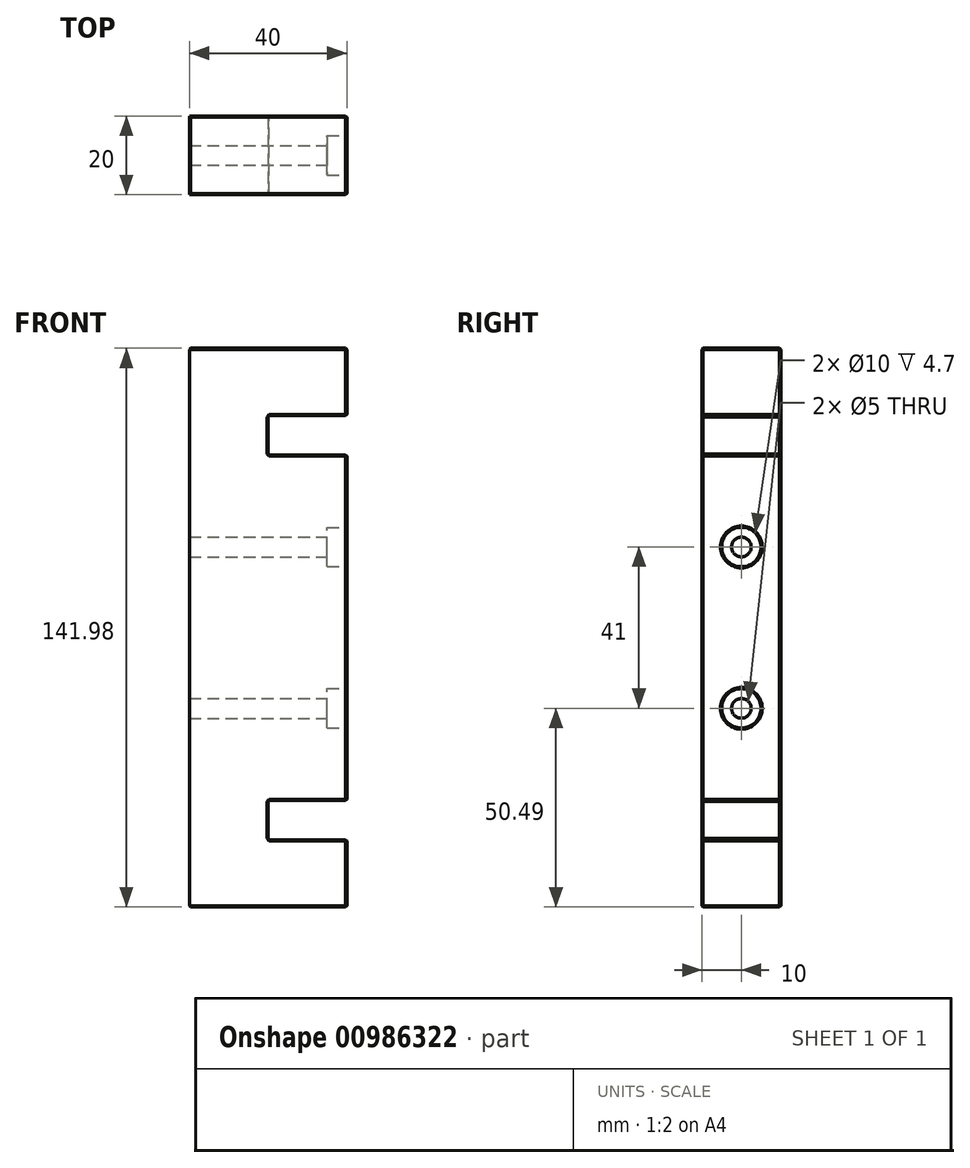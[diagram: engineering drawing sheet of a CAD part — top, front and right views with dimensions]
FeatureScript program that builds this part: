
annotation { "Feature Type Name" : "Feature", "Feature Type Description" : "" }
export const myFeature = defineFeature(function(context is Context, id is Id, definition is map)
    precondition{}
    {
        {
            var Q0;
            Q0=qCreatedBy(makeId("Right.planeOp"),FACE);
            var sketch = newSketch(context, id + "F0", { "sketchPlane" : qUnion([Q0])});
            skLineSegment(sketch, "E0", {"start": v(0, 0) * mm, "end": v(10, 0) * mm});
            skLineSegment(sketch, "E1", {"start": v(10, 0) * mm, "end": v(10, 141.98) * mm});
            skLineSegment(sketch, "E2", {"start": v(10, 141.98) * mm, "end": v(-10, 141.98) * mm});
            skLineSegment(sketch, "E3", {"start": v(-10, 141.98) * mm, "end": v(-10, 0) * mm});
            skLineSegment(sketch, "E4", {"start": v(-10, 0) * mm, "end": v(0, 0) * mm});
            skSolve(sketch);
        }
        {
            var Q0;
            Q0=makeQuery(id+"F0.imprint","IMPRINT",FACE,{"disambiguationData":[TD([[makeQuery(id+"F0.imprint","IMPRINT",EDGE,{"derivedFrom":sQuery(id+"F0.wireOp",EDGE,"E0")}),1.0]])]});
            extrude(context, id + "F1", {"entities" : qUnion([Q0]), "oppositeDirection" : true, "depth" : 40 * mm, "offsetDistance" : 25 * mm});
        }
        {
            var Q0;
            Q0=qCreatedBy(makeId("Right.planeOp"),FACE);
            var sketch = newSketch(context, id + "F2", { "sketchPlane" : qUnion([Q0])});
            skLineSegment(sketch, "E5", {"start": v(0, 0) * mm, "end": v(0, 50.5) * mm});
            skLineSegment(sketch, "E6", {"start": v(0, 50.5) * mm, "end": v(0, 91.49) * mm});
            skCircle(sketch, "E7", {"center": v(0, 50.5) * mm, "radius": 5 * mm});
            skCircle(sketch, "E8", {"center": v(0, 91.49) * mm, "radius": 5 * mm});
            skCircle(sketch, "E9", {"center": v(0, 91.49) * mm, "radius": 2.5 * mm});
            skCircle(sketch, "E10", {"center": v(0, 50.5) * mm, "radius": 2.5 * mm});
            skSolve(sketch);
        }
        {
            var Q0;
            Q0=makeQuery(id+"F2.imprint","IMPRINT",FACE,{"disambiguationData":[TD([[makeQuery(id+"F2.imprint","IMPRINT",EDGE,{"derivedFrom":sQuery(id+"F2.wireOp",EDGE,"E8")}),1.0]])]});
            var Q1;
            {var subQ0=sQuery(id+"F2.wireOp",EDGE,"E7");var subQ1=sQuery(id+"F2.wireOp",EDGE,"E5");var subQ2=makeQuery(id+"F2.imprint","INTERSECT",VERTEX,{"derivedFrom":[subQ1,subQ0]});Q1=makeQuery(id+"F2.imprint","IMPRINT",FACE,{"disambiguationData":[TD([[makeQuery(id+"F2.imprint","IMPRINT",EDGE,{"disambiguationData":[TD([[subQ2,-1.0]])],"derivedFrom":subQ1}),-1.0]])]});}
            var Q2;
            {var subQ0=sQuery(id+"F2.wireOp",EDGE,"E7");var subQ1=sQuery(id+"F2.wireOp",EDGE,"E5");var subQ2=makeQuery(id+"F2.imprint","INTERSECT",VERTEX,{"derivedFrom":[subQ1,subQ0]});Q2=makeQuery(id+"F2.imprint","IMPRINT",FACE,{"disambiguationData":[TD([[makeQuery(id+"F2.imprint","IMPRINT",EDGE,{"disambiguationData":[TD([[subQ2,-1.0]])],"derivedFrom":subQ1}),1.0]])]});}
            extrude(context, id + "F3", {"entities" : qUnion([Q0, Q1, Q2]), "operationType" : NewBodyOperationType.REMOVE, "oppositeDirection" : true, "depth" : 5 * mm, "offsetDistance" : 25 * mm});
        }
        {
            var Q0;
            Q0=makeQuery(id+"F3.boolean.opBoolean","SPLIT",FACE,{"disambiguationData":[TD([makeQuery(id+"F3.opExtrude","SWEPT_FACE",FACE,{"disambiguationData":[OSD([sQuery(id+"F2.wireOp",EDGE,"E9")])]})])],"derivedFrom":makeQuery(id+"F1.opExtrude","CAP_FACE",FACE,{"disambiguationData":[OSD([sQuery(id+"F0.wireOp",EDGE,"E0"),sQuery(id+"F0.wireOp",EDGE,"E1"),sQuery(id+"F0.wireOp",EDGE,"E2"),sQuery(id+"F0.wireOp",EDGE,"E3"),sQuery(id+"F0.wireOp",EDGE,"E4")])],"isStart":true})});
            var Q1;
            Q1=makeQuery(id+"F3.boolean.opBoolean","SPLIT",FACE,{"disambiguationData":[TD([makeQuery(id+"F3.opExtrude","SWEPT_FACE",FACE,{"disambiguationData":[OSD([sQuery(id+"F2.wireOp",EDGE,"E10")])]})])],"derivedFrom":makeQuery(id+"F1.opExtrude","CAP_FACE",FACE,{"disambiguationData":[OSD([sQuery(id+"F0.wireOp",EDGE,"E0"),sQuery(id+"F0.wireOp",EDGE,"E1"),sQuery(id+"F0.wireOp",EDGE,"E2"),sQuery(id+"F0.wireOp",EDGE,"E3"),sQuery(id+"F0.wireOp",EDGE,"E4")])],"isStart":true})});
            extrude(context, id + "F4", {"entities" : qUnion([Q0, Q1]), "operationType" : NewBodyOperationType.REMOVE, "endBound" : BoundingType.THROUGH_ALL, "oppositeDirection" : true, "depth" : 25 * mm, "offsetDistance" : 25 * mm});
        }
        {
            var Q0;
            Q0=makeQuery(id+"F1.opExtrude","SWEPT_FACE",FACE,{"disambiguationData":[OSD([sQuery(id+"F0.wireOp",EDGE,"E3")])]});
            cPlane(context, id + "F5", {"entities" : qUnion([Q0]), "cplaneType" : CPlaneType.OFFSET, "offset" : 0 * mm, "width" : 150 * mm, "height" : 150 * mm});
        }
        {
            var Q0;
            Q0=qCreatedBy(id+"F5.planeOp",FACE);
            var sketch = newSketch(context, id + "F6", { "sketchPlane" : qUnion([Q0])});
            skLineSegment(sketch, "E11", {"start": v(0, 0) * mm, "end": v(0, 17.1) * mm});
            skLineSegment(sketch, "E12", {"start": v(0, 17.1) * mm, "end": v(-20, 17.1) * mm});
            skLineSegment(sketch, "E13", {"start": v(-20, 17.1) * mm, "end": v(-20, 27.1) * mm});
            skLineSegment(sketch, "E14", {"start": v(-20, 27.1) * mm, "end": v(0, 27.1) * mm});
            skLineSegment(sketch, "E15", {"start": v(0, 114.86) * mm, "end": v(-20, 114.86) * mm});
            skLineSegment(sketch, "E16", {"start": v(-20, 114.86) * mm, "end": v(-20, 124.86) * mm});
            skLineSegment(sketch, "E17", {"start": v(-20, 124.86) * mm, "end": v(0, 124.86) * mm});
            skLineSegment(sketch, "E18", {"start": v(0, 27.1) * mm, "end": v(0, 114.86) * mm});
            skLineSegment(sketch, "E19", {"start": v(0, 114.86) * mm, "end": v(0, 124.86) * mm});
            skLineSegment(sketch, "E20", {"start": v(0, 17.1) * mm, "end": v(0, 27.1) * mm});
            skSolve(sketch);
        }
        {
            var Q0;
            Q0=makeQuery(id+"F6.imprint","IMPRINT",FACE,{"disambiguationData":[TD([[makeQuery(id+"F6.imprint","IMPRINT",EDGE,{"derivedFrom":sQuery(id+"F6.wireOp",EDGE,"E15")}),-1.0]])]});
            var Q1;
            Q1=makeQuery(id+"F6.imprint","IMPRINT",FACE,{"disambiguationData":[TD([[makeQuery(id+"F6.imprint","IMPRINT",EDGE,{"derivedFrom":sQuery(id+"F6.wireOp",EDGE,"E12")}),-1.0]])]});
            extrude(context, id + "F7", {"entities" : qUnion([Q0, Q1]), "operationType" : NewBodyOperationType.REMOVE, "oppositeDirection" : true, "depth" : 25 * mm, "offsetDistance" : 25 * mm});
        }
        {
            var Q0;
            {var subQ0=sQuery(id+"F0.wireOp",EDGE,"E4");var subQ1=sQuery(id+"F0.wireOp",EDGE,"E0");var subQ3=sQuery(id+"F0.wireOp",EDGE,"E1");var subQ4=makeQuery(id+"F1.opExtrude","SWEPT_FACE",FACE,{"disambiguationData":[OSD([subQ3])]});var subQ5=sQuery(id+"F0.wireOp",EDGE,"E3");var subQ7=sQuery(id+"F0.wireOp",EDGE,"E2");Q0=makeQuery(id+"F7.boolean.opBoolean","SPLIT",FACE,{"disambiguationData":[TD([makeQuery(id+"F7.opExtrude","SWEPT_FACE",FACE,{"disambiguationData":[OSD([sQuery(id+"F6.wireOp",EDGE,"E12")])]})])],"derivedFrom":makeQuery(id+"F3.boolean.opBoolean","SPLIT",FACE,{"disambiguationData":[TD([subQ4])],"derivedFrom":makeQuery(id+"F1.opExtrude","CAP_FACE",FACE,{"disambiguationData":[OSD([subQ1,subQ3,subQ7,subQ5,subQ0])],"isStart":true})})});}
            var Q1;
            {var subQ1=makeQuery(id+"F3.opExtrude","SWEPT_FACE",FACE,{"disambiguationData":[OSD([sQuery(id+"F2.wireOp",EDGE,"E7")])]});var subQ2=sQuery(id+"F0.wireOp",EDGE,"E3");var subQ4=sQuery(id+"F0.wireOp",EDGE,"E1");var subQ5=makeQuery(id+"F1.opExtrude","SWEPT_FACE",FACE,{"disambiguationData":[OSD([subQ4])]});var subQ6=sQuery(id+"F0.wireOp",EDGE,"E2");var subQ7=sQuery(id+"F0.wireOp",EDGE,"E4");var subQ8=sQuery(id+"F0.wireOp",EDGE,"E0");Q1=makeQuery(id+"F7.boolean.opBoolean","SPLIT",FACE,{"disambiguationData":[TD([makeQuery(id+"F3.boolean.opBoolean","COPY",FACE,{"derivedFrom":subQ1})])],"derivedFrom":makeQuery(id+"F3.boolean.opBoolean","SPLIT",FACE,{"disambiguationData":[TD([subQ5])],"derivedFrom":makeQuery(id+"F1.opExtrude","CAP_FACE",FACE,{"disambiguationData":[OSD([subQ8,subQ4,subQ6,subQ2,subQ7])],"isStart":true})})});}
            var Q2;
            {var subQ0=sQuery(id+"F0.wireOp",EDGE,"E1");var subQ1=makeQuery(id+"F1.opExtrude","SWEPT_FACE",FACE,{"disambiguationData":[OSD([subQ0])]});var subQ2=sQuery(id+"F0.wireOp",EDGE,"E2");var subQ3=makeQuery(id+"F1.opExtrude","SWEPT_FACE",FACE,{"disambiguationData":[OSD([subQ2])]});var subQ4=sQuery(id+"F0.wireOp",EDGE,"E3");var subQ6=sQuery(id+"F0.wireOp",EDGE,"E4");var subQ7=sQuery(id+"F0.wireOp",EDGE,"E0");Q2=makeQuery(id+"F7.boolean.opBoolean","SPLIT",FACE,{"disambiguationData":[TD([subQ3])],"derivedFrom":makeQuery(id+"F3.boolean.opBoolean","SPLIT",FACE,{"disambiguationData":[TD([subQ1])],"derivedFrom":makeQuery(id+"F1.opExtrude","CAP_FACE",FACE,{"disambiguationData":[OSD([subQ7,subQ0,subQ2,subQ4,subQ6])],"isStart":true})})});}
            var Q3;
            Q3=makeQuery(id+"F1.opExtrude","SWEPT_FACE",FACE,{"disambiguationData":[OSD([sQuery(id+"F0.wireOp",EDGE,"E0"),sQuery(id+"F0.wireOp",EDGE,"E4")])]});
            var Q4;
            Q4=makeQuery(id+"F1.opExtrude","SWEPT_FACE",FACE,{"disambiguationData":[OSD([sQuery(id+"F0.wireOp",EDGE,"E2")])]});
            var Q5;
            Q5=makeQuery(id+"F7.boolean.opBoolean","COPY",FACE,{"derivedFrom":makeQuery(id+"F7.opExtrude","SWEPT_FACE",FACE,{"disambiguationData":[OSD([sQuery(id+"F6.wireOp",EDGE,"E17")])]})});
            var Q6;
            Q6=makeQuery(id+"F7.boolean.opBoolean","COPY",EDGE,{"derivedFrom":makeQuery(id+"F7.opExtrude","SWEPT_EDGE",EDGE,{"disambiguationData":[OSD([sQuery(id+"F6.wireOp",EDGE,"E15"),sQuery(id+"F6.wireOp",EDGE,"E16")])]})});
            var Q7;
            Q7=makeQuery(id+"F7.boolean.opBoolean","COPY",FACE,{"derivedFrom":makeQuery(id+"F7.opExtrude","SWEPT_FACE",FACE,{"disambiguationData":[OSD([sQuery(id+"F6.wireOp",EDGE,"E15")])]})});
            var Q8;
            Q8=makeQuery(id+"F7.boolean.opBoolean","COPY",FACE,{"derivedFrom":makeQuery(id+"F7.opExtrude","SWEPT_FACE",FACE,{"disambiguationData":[OSD([sQuery(id+"F6.wireOp",EDGE,"E14")])]})});
            var Q9;
            Q9=makeQuery(id+"F7.boolean.opBoolean","COPY",FACE,{"derivedFrom":makeQuery(id+"F7.opExtrude","SWEPT_FACE",FACE,{"disambiguationData":[OSD([sQuery(id+"F6.wireOp",EDGE,"E12")])]})});
            chamfer(context, id + "F8", {"entities" : qUnion([Q0, Q1, Q2, Q3, Q4, Q5, Q6, Q7, Q8, Q9]), "width" : 0.3 * mm, "tangentPropagation" : true});
        }
    });
